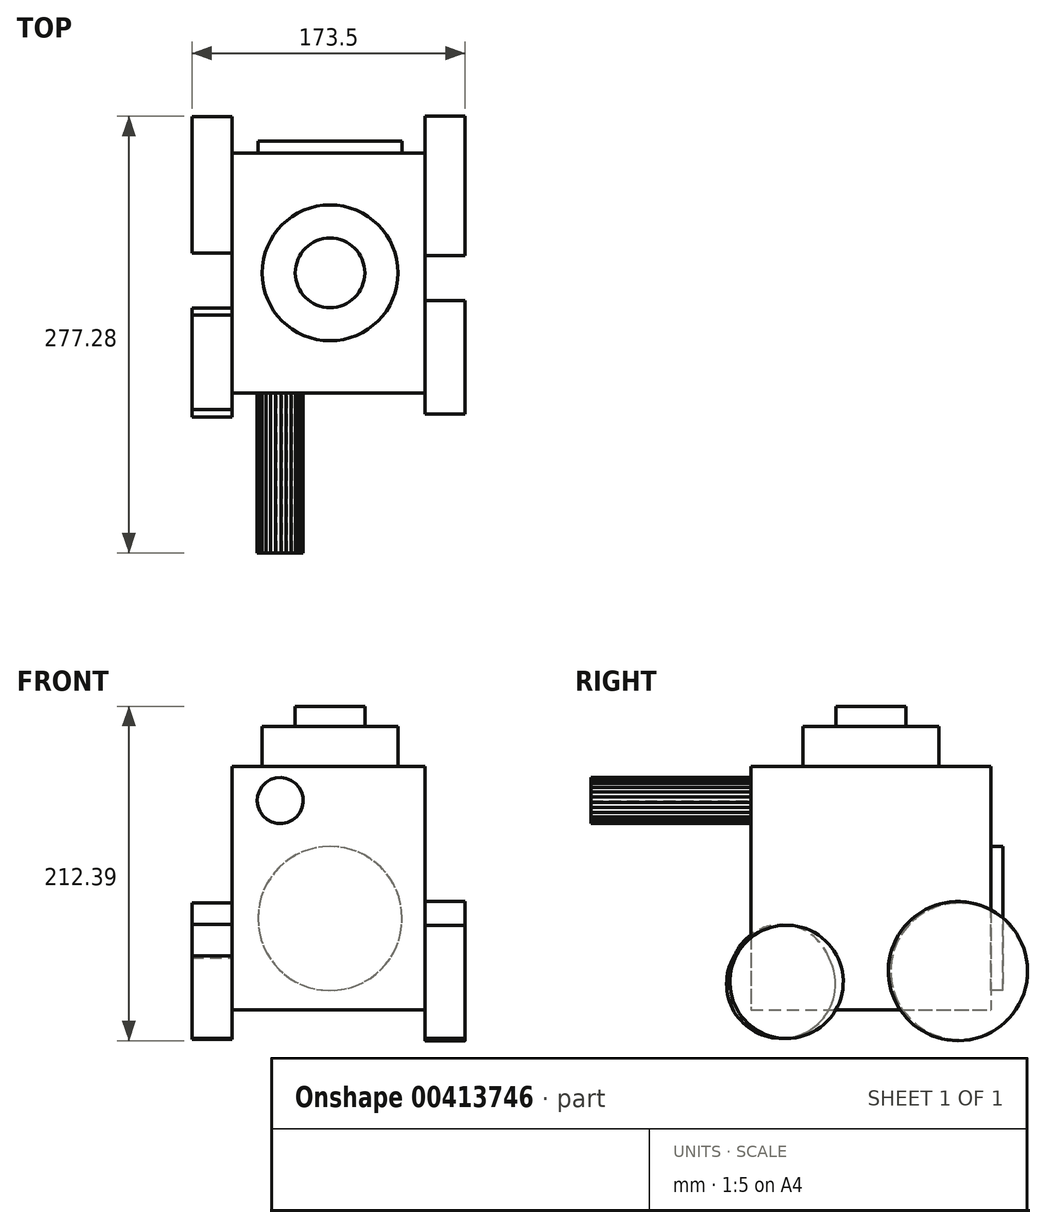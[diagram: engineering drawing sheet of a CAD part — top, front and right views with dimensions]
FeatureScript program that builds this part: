
annotation { "Feature Type Name" : "Feature", "Feature Type Description" : "" }
export const myFeature = defineFeature(function(context is Context, id is Id, definition is map)
    precondition{}
    {
        {
            var Q0;
            Q0=qCreatedBy(makeId("Front.planeOp"),FACE);
            var sketch = newSketch(context, id + "F0", { "sketchPlane" : qUnion([Q0])});
            skCircle(sketch, "E0.cCircle", {"center": v(-31.62, 38.1) * mm, "radius": 14.6 * mm, "construction": true});
            skLineSegment(sketch, "E0.0", {"start": v(-45.72, 34.3) * mm, "end": v(-46.22, 37.66) * mm});
            skLineSegment(sketch, "E0.1", {"start": v(-46.22, 37.66) * mm, "end": v(-45.92, 41.04) * mm});
            skLineSegment(sketch, "E0.2", {"start": v(-45.92, 41.04) * mm, "end": v(-44.86, 44.26) * mm});
            skLineSegment(sketch, "E0.3", {"start": v(-44.86, 44.26) * mm, "end": v(-43.08, 47.15) * mm});
            skLineSegment(sketch, "E0.4", {"start": v(-43.08, 47.15) * mm, "end": v(-40.69, 49.54) * mm});
            skLineSegment(sketch, "E0.5", {"start": v(-40.69, 49.54) * mm, "end": v(-37.8, 51.33) * mm});
            skLineSegment(sketch, "E0.6", {"start": v(-37.8, 51.33) * mm, "end": v(-34.58, 52.4) * mm});
            skLineSegment(sketch, "E0.7", {"start": v(-34.58, 52.4) * mm, "end": v(-31.2, 52.7) * mm});
            skLineSegment(sketch, "E0.8", {"start": v(-31.2, 52.7) * mm, "end": v(-27.85, 52.2) * mm});
            skLineSegment(sketch, "E0.9", {"start": v(-27.85, 52.2) * mm, "end": v(-24.7, 50.96) * mm});
            skLineSegment(sketch, "E0.10", {"start": v(-24.7, 50.96) * mm, "end": v(-21.92, 49.01) * mm});
            skLineSegment(sketch, "E0.11", {"start": v(-21.92, 49.01) * mm, "end": v(-19.66, 46.48) * mm});
            skLineSegment(sketch, "E0.12", {"start": v(-19.66, 46.48) * mm, "end": v(-18.05, 43.5) * mm});
            skLineSegment(sketch, "E0.13", {"start": v(-18.05, 43.5) * mm, "end": v(-17.17, 40.22) * mm});
            skLineSegment(sketch, "E0.14", {"start": v(-17.17, 40.22) * mm, "end": v(-17.07, 36.84) * mm});
            skLineSegment(sketch, "E0.15", {"start": v(-17.07, 36.84) * mm, "end": v(-17.75, 33.51) * mm});
            skLineSegment(sketch, "E0.16", {"start": v(-17.75, 33.51) * mm, "end": v(-19.18, 30.44) * mm});
            skLineSegment(sketch, "E0.17", {"start": v(-19.18, 30.44) * mm, "end": v(-21.28, 27.78) * mm});
            skLineSegment(sketch, "E0.18", {"start": v(-21.28, 27.78) * mm, "end": v(-23.94, 25.67) * mm});
            skLineSegment(sketch, "E0.19", {"start": v(-23.94, 25.67) * mm, "end": v(-27.01, 24.24) * mm});
            skLineSegment(sketch, "E0.20", {"start": v(-27.01, 24.24) * mm, "end": v(-30.33, 23.55) * mm});
            skLineSegment(sketch, "E0.21", {"start": v(-30.33, 23.55) * mm, "end": v(-33.72, 23.64) * mm});
            skLineSegment(sketch, "E0.22", {"start": v(-33.72, 23.64) * mm, "end": v(-37, 24.52) * mm});
            skLineSegment(sketch, "E0.23", {"start": v(-37, 24.52) * mm, "end": v(-39.99, 26.13) * mm});
            skLineSegment(sketch, "E0.24", {"start": v(-39.99, 26.13) * mm, "end": v(-42.52, 28.38) * mm});
            skLineSegment(sketch, "E0.25", {"start": v(-42.52, 28.38) * mm, "end": v(-44.47, 31.15) * mm});
            skLineSegment(sketch, "E0.26", {"start": v(-44.47, 31.15) * mm, "end": v(-45.72, 34.3) * mm});
            skSolve(sketch);
        }
        {
            var Q0;
            Q0=makeQuery(id+"F0.imprint","IMPRINT",FACE,{"disambiguationData":[TD([[makeQuery(id+"F0.imprint","IMPRINT",EDGE,{"derivedFrom":sQuery(id+"F0.wireOp",EDGE,"E0.0")}),-1.0]])]});
            extrude(context, id + "F1", {"entities" : qUnion([Q0]), "depth" : 25.4 * mm});
        }
        {
            var Q0;
            Q0=makeQuery(id+"F1.opExtrude","CAP_FACE",FACE,{"disambiguationData":[OSD([sQuery(id+"F0.wireOp",EDGE,"E0.0"),sQuery(id+"F0.wireOp",EDGE,"E0.1"),sQuery(id+"F0.wireOp",EDGE,"E0.2"),sQuery(id+"F0.wireOp",EDGE,"E0.3"),sQuery(id+"F0.wireOp",EDGE,"E0.4"),sQuery(id+"F0.wireOp",EDGE,"E0.5"),sQuery(id+"F0.wireOp",EDGE,"E0.6"),sQuery(id+"F0.wireOp",EDGE,"E0.7"),sQuery(id+"F0.wireOp",EDGE,"E0.8"),sQuery(id+"F0.wireOp",EDGE,"E0.9"),sQuery(id+"F0.wireOp",EDGE,"E0.10"),sQuery(id+"F0.wireOp",EDGE,"E0.11"),sQuery(id+"F0.wireOp",EDGE,"E0.12"),sQuery(id+"F0.wireOp",EDGE,"E0.13"),sQuery(id+"F0.wireOp",EDGE,"E0.14"),sQuery(id+"F0.wireOp",EDGE,"E0.15"),sQuery(id+"F0.wireOp",EDGE,"E0.16"),sQuery(id+"F0.wireOp",EDGE,"E0.17"),sQuery(id+"F0.wireOp",EDGE,"E0.18"),sQuery(id+"F0.wireOp",EDGE,"E0.19"),sQuery(id+"F0.wireOp",EDGE,"E0.20"),sQuery(id+"F0.wireOp",EDGE,"E0.21"),sQuery(id+"F0.wireOp",EDGE,"E0.22"),sQuery(id+"F0.wireOp",EDGE,"E0.23"),sQuery(id+"F0.wireOp",EDGE,"E0.24"),sQuery(id+"F0.wireOp",EDGE,"E0.25"),sQuery(id+"F0.wireOp",EDGE,"E0.26")])],"isStart":false});
            extrude(context, id + "F2", {"entities" : qUnion([Q0]), "operationType" : NewBodyOperationType.ADD, "depth" : 127 * mm});
        }
        {
            var Q0;
            Q0=qCreatedBy(makeId("Front.planeOp"),FACE);
            var sketch = newSketch(context, id + "F3", { "sketchPlane" : qUnion([Q0])});
            skLineSegment(sketch, "E1.bottom", {"start": v(-73.07, 73.14) * mm, "end": v(-62.37, 73.14) * mm});
            skLineSegment(sketch, "E1.top", {"start": v(-73.07, 59.81) * mm, "end": v(-62.37, 59.81) * mm});
            skLineSegment(sketch, "E1.left", {"start": v(-73.07, 73.14) * mm, "end": v(-73.07, 59.81) * mm});
            skLineSegment(sketch, "E1.right", {"start": v(-62.37, 73.14) * mm, "end": v(-62.37, 59.81) * mm});
            skLineSegment(sketch, "E2.bottom", {"start": v(-62.37, 59.81) * mm, "end": v(60.33, 59.81) * mm});
            skLineSegment(sketch, "E2.top", {"start": v(-62.37, -69.44) * mm, "end": v(60.33, -69.44) * mm});
            skLineSegment(sketch, "E2.left", {"start": v(-62.37, 59.81) * mm, "end": v(-62.37, -69.44) * mm});
            skLineSegment(sketch, "E2.right", {"start": v(60.33, 59.81) * mm, "end": v(60.33, -69.44) * mm});
            skSolve(sketch);
        }
        {
            var Q0;
            Q0=makeQuery(id+"F3.imprint","IMPRINT",FACE,{"disambiguationData":[TD([[makeQuery(id+"F3.imprint","IMPRINT",EDGE,{"derivedFrom":sQuery(id+"F3.wireOp",EDGE,"E2.bottom")}),-1.0]])]});
            extrude(context, id + "F4", {"entities" : qUnion([Q0]), "operationType" : NewBodyOperationType.ADD, "depth" : 76.2 * mm});
        }
        {
            var Q0;
            Q0=makeQuery(id+"F4.boolean.opBoolean","MERGE",FACE,{"derivedFrom":[makeQuery(id+"F1.opExtrude","CAP_FACE",FACE,{"disambiguationData":[OSD([sQuery(id+"F0.wireOp",EDGE,"E0.0"),sQuery(id+"F0.wireOp",EDGE,"E0.1"),sQuery(id+"F0.wireOp",EDGE,"E0.2"),sQuery(id+"F0.wireOp",EDGE,"E0.3"),sQuery(id+"F0.wireOp",EDGE,"E0.4"),sQuery(id+"F0.wireOp",EDGE,"E0.5"),sQuery(id+"F0.wireOp",EDGE,"E0.6"),sQuery(id+"F0.wireOp",EDGE,"E0.7"),sQuery(id+"F0.wireOp",EDGE,"E0.8"),sQuery(id+"F0.wireOp",EDGE,"E0.9"),sQuery(id+"F0.wireOp",EDGE,"E0.10"),sQuery(id+"F0.wireOp",EDGE,"E0.11"),sQuery(id+"F0.wireOp",EDGE,"E0.12"),sQuery(id+"F0.wireOp",EDGE,"E0.13"),sQuery(id+"F0.wireOp",EDGE,"E0.14"),sQuery(id+"F0.wireOp",EDGE,"E0.15"),sQuery(id+"F0.wireOp",EDGE,"E0.16"),sQuery(id+"F0.wireOp",EDGE,"E0.17"),sQuery(id+"F0.wireOp",EDGE,"E0.18"),sQuery(id+"F0.wireOp",EDGE,"E0.19"),sQuery(id+"F0.wireOp",EDGE,"E0.20"),sQuery(id+"F0.wireOp",EDGE,"E0.21"),sQuery(id+"F0.wireOp",EDGE,"E0.22"),sQuery(id+"F0.wireOp",EDGE,"E0.23"),sQuery(id+"F0.wireOp",EDGE,"E0.24"),sQuery(id+"F0.wireOp",EDGE,"E0.25"),sQuery(id+"F0.wireOp",EDGE,"E0.26")])],"isStart":true}),makeQuery(id+"F4.opExtrude","CAP_FACE",FACE,{"disambiguationData":[OSD([sQuery(id+"F3.wireOp",EDGE,"E2.bottom"),sQuery(id+"F3.wireOp",EDGE,"E2.top"),sQuery(id+"F3.wireOp",EDGE,"E2.left"),sQuery(id+"F3.wireOp",EDGE,"E2.right")])],"isStart":true})]});
            extrude(context, id + "F5", {"entities" : qUnion([Q0]), "operationType" : NewBodyOperationType.ADD, "depth" : 76.2 * mm});
        }
        {
            var Q0;
            {var subQ0=sQuery(id+"F3.wireOp",EDGE,"E2.top");Q0=makeQuery(id+"F5.boolean.opBoolean","MERGE",FACE,{"derivedFrom":[makeQuery(id+"F4.opExtrude","SWEPT_FACE",FACE,{"disambiguationData":[OSD([subQ0])]}),makeQuery(id+"F5.opExtrude","SWEPT_FACE",FACE,{"disambiguationData":[OSD([subQ0])]})]});}
            extrude(context, id + "F6", {"entities" : qUnion([Q0]), "operationType" : NewBodyOperationType.ADD, "depth" : 25.4 * mm});
        }
        {
            var Q0;
            {var subQ0=sQuery(id+"F3.wireOp",EDGE,"E2.right");Q0=makeQuery(id+"F6.boolean.opBoolean","MERGE",FACE,{"derivedFrom":[makeQuery(id+"F5.boolean.opBoolean","MERGE",FACE,{"derivedFrom":[makeQuery(id+"F4.opExtrude","SWEPT_FACE",FACE,{"disambiguationData":[OSD([subQ0])]}),makeQuery(id+"F5.opExtrude","SWEPT_FACE",FACE,{"disambiguationData":[OSD([subQ0])]})]}),makeQuery(id+"F6.opExtrude","SWEPT_FACE",FACE,{"disambiguationData":[OSD([sQuery(id+"F3.wireOp",EDGE,"E2.top"),subQ0])]})]});}
            var sketch = newSketch(context, id + "F7", { "sketchPlane" : qUnion([Q0])});
            skCircle(sketch, "E3", {"center": v(-53.58, -77.12) * mm, "radius": 35.98 * mm});
            skSolve(sketch);
        }
        {
            var Q0;
            Q0 = qSketchRegion(id + "F7", true);
            extrude(context, id + "F8", {"entities" : qUnion([Q0]), "operationType" : NewBodyOperationType.ADD, "depth" : 25.4 * mm});
        }
        {
            var Q0;
            {var subQ0=sQuery(id+"F3.wireOp",EDGE,"E2.right");Q0=makeQuery(id+"F6.boolean.opBoolean","MERGE",FACE,{"derivedFrom":[makeQuery(id+"F5.boolean.opBoolean","MERGE",FACE,{"derivedFrom":[makeQuery(id+"F4.opExtrude","SWEPT_FACE",FACE,{"disambiguationData":[OSD([subQ0])]}),makeQuery(id+"F5.opExtrude","SWEPT_FACE",FACE,{"disambiguationData":[OSD([subQ0])]})]}),makeQuery(id+"F6.opExtrude","SWEPT_FACE",FACE,{"disambiguationData":[OSD([sQuery(id+"F3.wireOp",EDGE,"E2.top"),subQ0])]})]});}
            var sketch = newSketch(context, id + "F9", { "sketchPlane" : qUnion([Q0])});
            skCircle(sketch, "E4", {"center": v(55.27, -70.27) * mm, "radius": 44.21 * mm});
            skSolve(sketch);
        }
        {
            var Q0;
            Q0 = qSketchRegion(id + "F9", true);
            extrude(context, id + "F10", {"entities" : qUnion([Q0]), "operationType" : NewBodyOperationType.ADD, "depth" : 25.4 * mm});
        }
        {
            var Q0;
            {var subQ0=sQuery(id+"F3.wireOp",EDGE,"E2.right");Q0=makeQuery(id+"F6.boolean.opBoolean","MERGE",FACE,{"derivedFrom":[makeQuery(id+"F5.boolean.opBoolean","MERGE",FACE,{"derivedFrom":[makeQuery(id+"F4.opExtrude","SWEPT_FACE",FACE,{"disambiguationData":[OSD([subQ0])]}),makeQuery(id+"F5.opExtrude","SWEPT_FACE",FACE,{"disambiguationData":[OSD([subQ0])]})]}),makeQuery(id+"F6.opExtrude","SWEPT_FACE",FACE,{"disambiguationData":[OSD([sQuery(id+"F3.wireOp",EDGE,"E2.top"),subQ0])]})]});}
            var sketch = newSketch(context, id + "F11", { "sketchPlane" : qUnion([Q0])});
            skSolve(sketch);
        }
        {
            var Q0;
            {var subQ0=sQuery(id+"F3.wireOp",EDGE,"E2.left");Q0=makeQuery(id+"F6.boolean.opBoolean","MERGE",FACE,{"derivedFrom":[makeQuery(id+"F5.boolean.opBoolean","MERGE",FACE,{"derivedFrom":[makeQuery(id+"F4.opExtrude","SWEPT_FACE",FACE,{"disambiguationData":[OSD([subQ0])]}),makeQuery(id+"F5.opExtrude","SWEPT_FACE",FACE,{"disambiguationData":[OSD([subQ0])]})]}),makeQuery(id+"F6.opExtrude","SWEPT_FACE",FACE,{"disambiguationData":[OSD([sQuery(id+"F3.wireOp",EDGE,"E2.top"),subQ0])]})]});}
            var sketch = newSketch(context, id + "F12", { "sketchPlane" : qUnion([Q0])});
            skCircle(sketch, "E5", {"center": v(56.97, -73) * mm, "radius": 32.23 * mm});
            skSolve(sketch);
        }
        {
            var Q0;
            {var subQ0=sQuery(id+"F3.wireOp",EDGE,"E2.left");var subQ1=sQuery(id+"F3.wireOp",EDGE,"E2.top");var subQ2=makeQuery(id+"F6.boolean.opBoolean","MERGE",EDGE,{"derivedFrom":[makeQuery(id+"F5.opExtrude","CAP_EDGE",EDGE,{"disambiguationData":[OSD([subQ0])],"isStart":false}),makeQuery(id+"F6.opExtrude","SWEPT_EDGE",EDGE,{"disambiguationData":[OSD([subQ1,subQ0]),TDD([makeQuery(id+"F5.opExtrude","CAP_VERTEX",VERTEX,{"disambiguationData":[OSD([subQ1,subQ0])],"isStart":false})])]})]});Q0=makeQuery(id+"F12.imprint","IMPRINT",FACE,{"disambiguationData":[TD([[makeQuery(id+"F12.imprint","IMPRINT",EDGE,{"derivedFrom":subQ2}),1.0]])]});}
            var sketch = newSketch(context, id + "F13", { "sketchPlane" : qUnion([Q0])});
            skCircle(sketch, "E6", {"center": v(57.09, -78.47) * mm, "radius": 34.58 * mm});
            skSolve(sketch);
        }
        {
            var Q0;
            Q0 = qSketchRegion(id + "F13", true);
            var Q1;
            {var subQ0=sQuery(id+"F13.wireOp",EDGE,"E6");var subQ1=sQuery(id+"F12.wireOp",EDGE,"E5");var subQ2=sQuery(id+"F3.wireOp",EDGE,"E2.left");var subQ3=sQuery(id+"F3.wireOp",EDGE,"E2.top");var subQ4=makeQuery(id+"F6.opExtrude","CAP_EDGE",EDGE,{"disambiguationData":[OSD([subQ3,subQ2])],"isStart":false});var subQ5=makeQuery(id+"F12.imprint","INTERSECT",VERTEX,{"derivedFrom":[subQ4,subQ1]});var subQ6=makeQuery(id+"F12.imprint","IMPRINT",EDGE,{"disambiguationData":[TD([[subQ5,1.0]])],"derivedFrom":subQ1});var subQ7=makeQuery(id+"F13.imprint","INTERSECT",VERTEX,{"derivedFrom":[subQ6,subQ0]});Q1=makeQuery(id+"F13.imprint","IMPRINT",FACE,{"disambiguationData":[TD([[makeQuery(id+"F13.imprint","IMPRINT",EDGE,{"disambiguationData":[TD([[subQ7,1.0]])],"derivedFrom":subQ0}),1.0]])]});}
            var Q2;
            Q2 = qSketchRegion(id + "F12", true);
            var Q3;
            {var subQ0=sQuery(id+"F12.wireOp",EDGE,"E5");var subQ1=sQuery(id+"F3.wireOp",EDGE,"E2.left");var subQ2=sQuery(id+"F3.wireOp",EDGE,"E2.top");var subQ3=makeQuery(id+"F6.opExtrude","CAP_EDGE",EDGE,{"disambiguationData":[OSD([subQ2,subQ1])],"isStart":false});var subQ4=makeQuery(id+"F12.imprint","INTERSECT",VERTEX,{"derivedFrom":[subQ3,subQ0]});Q3=makeQuery(id+"F12.imprint","IMPRINT",FACE,{"disambiguationData":[TD([[makeQuery(id+"F12.imprint","IMPRINT",EDGE,{"disambiguationData":[TD([[subQ4,1.0]])],"derivedFrom":subQ0}),1.0]])]});}
            extrude(context, id + "F14", {"entities" : qUnion([Q0, Q1, Q2, Q3]), "operationType" : NewBodyOperationType.ADD, "depth" : 25.4 * mm});
        }
        {
            var Q0;
            {var subQ0=sQuery(id+"F3.wireOp",EDGE,"E2.left");Q0=makeQuery(id+"F6.boolean.opBoolean","MERGE",FACE,{"derivedFrom":[makeQuery(id+"F5.boolean.opBoolean","MERGE",FACE,{"derivedFrom":[makeQuery(id+"F4.opExtrude","SWEPT_FACE",FACE,{"disambiguationData":[OSD([subQ0])]}),makeQuery(id+"F5.opExtrude","SWEPT_FACE",FACE,{"disambiguationData":[OSD([subQ0])]})]}),makeQuery(id+"F6.opExtrude","SWEPT_FACE",FACE,{"disambiguationData":[OSD([sQuery(id+"F3.wireOp",EDGE,"E2.top"),subQ0])]})]});}
            var sketch = newSketch(context, id + "F15", { "sketchPlane" : qUnion([Q0])});
            skCircle(sketch, "E7", {"center": v(-55.86, -70.38) * mm, "radius": 43.3 * mm});
            skSolve(sketch);
        }
        {
            var Q0;
            Q0 = qSketchRegion(id + "F15", true);
            extrude(context, id + "F16", {"entities" : qUnion([Q0]), "operationType" : NewBodyOperationType.ADD, "depth" : 25.4 * mm});
        }
        {
            var Q0;
            {var subQ0=sQuery(id+"F3.wireOp",EDGE,"E2.bottom");Q0=makeQuery(id+"F5.boolean.opBoolean","MERGE",FACE,{"derivedFrom":[makeQuery(id+"F4.opExtrude","SWEPT_FACE",FACE,{"disambiguationData":[OSD([subQ0])]}),makeQuery(id+"F5.opExtrude","SWEPT_FACE",FACE,{"disambiguationData":[OSD([subQ0])]})]});}
            var sketch = newSketch(context, id + "F17", { "sketchPlane" : qUnion([Q0])});
            skCircle(sketch, "E8", {"center": v(0, 0) * mm, "radius": 43.15 * mm});
            skSolve(sketch);
        }
        {
            var Q0;
            Q0 = qSketchRegion(id + "F17", true);
            extrude(context, id + "F18", {"entities" : qUnion([Q0]), "operationType" : NewBodyOperationType.ADD, "depth" : 25.4 * mm});
        }
        {
            var Q0;
            Q0=makeQuery(id+"F18.opExtrude","CAP_FACE",FACE,{"disambiguationData":[OSD([sQuery(id+"F17.wireOp",EDGE,"E8")])],"isStart":false});
            var sketch = newSketch(context, id + "F19", { "sketchPlane" : qUnion([Q0])});
            skCircle(sketch, "E9", {"center": v(0, 0) * mm, "radius": 22.1 * mm});
            skSolve(sketch);
        }
        {
            var Q0;
            Q0 = qSketchRegion(id + "F19", true);
            extrude(context, id + "F20", {"entities" : qUnion([Q0]), "operationType" : NewBodyOperationType.ADD, "depth" : 12.7 * mm});
        }
        {
            var Q0;
            {var subQ0=sQuery(id+"F3.wireOp",EDGE,"E2.top");Q0=makeQuery(id+"F6.boolean.opBoolean","MERGE",FACE,{"derivedFrom":[makeQuery(id+"F5.opExtrude","CAP_FACE",FACE,{"disambiguationData":[OSD([sQuery(id+"F0.wireOp",EDGE,"E0.0"),sQuery(id+"F0.wireOp",EDGE,"E0.1"),sQuery(id+"F0.wireOp",EDGE,"E0.2"),sQuery(id+"F0.wireOp",EDGE,"E0.3"),sQuery(id+"F0.wireOp",EDGE,"E0.4"),sQuery(id+"F0.wireOp",EDGE,"E0.5"),sQuery(id+"F0.wireOp",EDGE,"E0.6"),sQuery(id+"F0.wireOp",EDGE,"E0.7"),sQuery(id+"F0.wireOp",EDGE,"E0.8"),sQuery(id+"F0.wireOp",EDGE,"E0.9"),sQuery(id+"F0.wireOp",EDGE,"E0.10"),sQuery(id+"F0.wireOp",EDGE,"E0.11"),sQuery(id+"F0.wireOp",EDGE,"E0.12"),sQuery(id+"F0.wireOp",EDGE,"E0.13"),sQuery(id+"F0.wireOp",EDGE,"E0.14"),sQuery(id+"F0.wireOp",EDGE,"E0.15"),sQuery(id+"F0.wireOp",EDGE,"E0.16"),sQuery(id+"F0.wireOp",EDGE,"E0.17"),sQuery(id+"F0.wireOp",EDGE,"E0.18"),sQuery(id+"F0.wireOp",EDGE,"E0.19"),sQuery(id+"F0.wireOp",EDGE,"E0.20"),sQuery(id+"F0.wireOp",EDGE,"E0.21"),sQuery(id+"F0.wireOp",EDGE,"E0.22"),sQuery(id+"F0.wireOp",EDGE,"E0.23"),sQuery(id+"F0.wireOp",EDGE,"E0.24"),sQuery(id+"F0.wireOp",EDGE,"E0.25"),sQuery(id+"F0.wireOp",EDGE,"E0.26"),sQuery(id+"F3.wireOp",EDGE,"E2.bottom"),subQ0,sQuery(id+"F3.wireOp",EDGE,"E2.left"),sQuery(id+"F3.wireOp",EDGE,"E2.right")])],"isStart":false}),makeQuery(id+"F6.opExtrude","SWEPT_FACE",FACE,{"disambiguationData":[OSD([subQ0]),TDD([makeQuery(id+"F5.opExtrude","CAP_EDGE",EDGE,{"disambiguationData":[OSD([subQ0])],"isStart":false})])]})]});}
            var sketch = newSketch(context, id + "F21", { "sketchPlane" : qUnion([Q0])});
            skCircle(sketch, "E10", {"center": v(0, -36.86) * mm, "radius": 45.74 * mm});
            skSolve(sketch);
        }
        {
            var Q0;
            Q0=makeQuery(id+"F21.imprint","IMPRINT",FACE,{"disambiguationData":[TD([[makeQuery(id+"F21.imprint","IMPRINT",EDGE,{"derivedFrom":sQuery(id+"F21.wireOp",EDGE,"E10")}),1.0]])]});
            extrude(context, id + "F22", {"entities" : qUnion([Q0]), "operationType" : NewBodyOperationType.ADD, "depth" : 7.62 * mm});
        }
        {
            var Q0;
            Q0=makeQuery(id+"F2.opExtrude","CAP_FACE",FACE,{"disambiguationData":[OSD([sQuery(id+"F0.wireOp",EDGE,"E0.0"),sQuery(id+"F0.wireOp",EDGE,"E0.1"),sQuery(id+"F0.wireOp",EDGE,"E0.2"),sQuery(id+"F0.wireOp",EDGE,"E0.3"),sQuery(id+"F0.wireOp",EDGE,"E0.4"),sQuery(id+"F0.wireOp",EDGE,"E0.5"),sQuery(id+"F0.wireOp",EDGE,"E0.6"),sQuery(id+"F0.wireOp",EDGE,"E0.7"),sQuery(id+"F0.wireOp",EDGE,"E0.8"),sQuery(id+"F0.wireOp",EDGE,"E0.9"),sQuery(id+"F0.wireOp",EDGE,"E0.10"),sQuery(id+"F0.wireOp",EDGE,"E0.11"),sQuery(id+"F0.wireOp",EDGE,"E0.12"),sQuery(id+"F0.wireOp",EDGE,"E0.13"),sQuery(id+"F0.wireOp",EDGE,"E0.14"),sQuery(id+"F0.wireOp",EDGE,"E0.15"),sQuery(id+"F0.wireOp",EDGE,"E0.16"),sQuery(id+"F0.wireOp",EDGE,"E0.17"),sQuery(id+"F0.wireOp",EDGE,"E0.18"),sQuery(id+"F0.wireOp",EDGE,"E0.19"),sQuery(id+"F0.wireOp",EDGE,"E0.20"),sQuery(id+"F0.wireOp",EDGE,"E0.21"),sQuery(id+"F0.wireOp",EDGE,"E0.22"),sQuery(id+"F0.wireOp",EDGE,"E0.23"),sQuery(id+"F0.wireOp",EDGE,"E0.24"),sQuery(id+"F0.wireOp",EDGE,"E0.25"),sQuery(id+"F0.wireOp",EDGE,"E0.26")])],"isStart":false});
            extrude(context, id + "F23", {"entities" : qUnion([Q0]), "operationType" : NewBodyOperationType.ADD, "depth" : 25.4 * mm});
        }
    });
